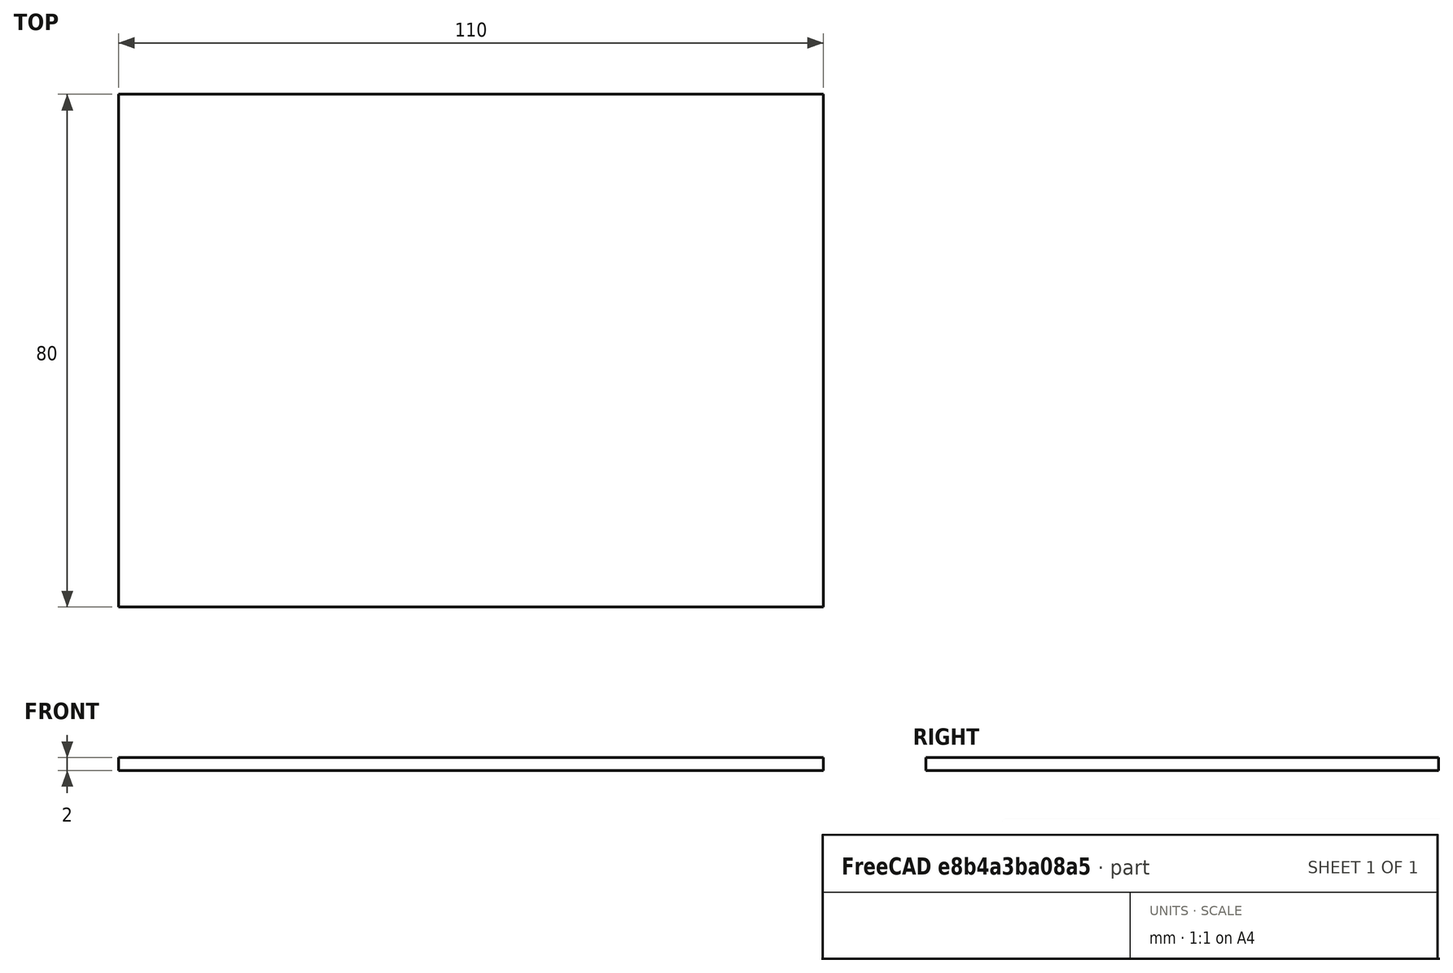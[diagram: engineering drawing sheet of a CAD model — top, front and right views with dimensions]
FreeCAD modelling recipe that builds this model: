
FCSTD DOCUMENT  (FreeCAD 0.18R16146 (Git))
Label: v_w-tapa-paso 1
License: All rights reserved
LicenseURL: http://en.wikipedia.org/wiki/All_rights_reserved
objects: Sketcher::SketchObject×1, PartDesign::Pad×1, PartDesign::Body×1
note: 4 computed .brp shape members not serialized (recipe doc carries the construction recipe); baked Part::Feature solids carry a one-line shape summary decoded from their .brp

FEATURE [Sketcher::SketchObject] Sketch
  MapMode = 5
  Support = -> [XY_Plane]
  sketch-geometry (4):
    g0: LineSegment StartX=-55 StartY=-40 StartZ=0 EndX=55 EndY=-40 EndZ=0
    g1: LineSegment StartX=55 StartY=-40 StartZ=0 EndX=55 EndY=40 EndZ=0
    g2: LineSegment StartX=55 StartY=40 StartZ=0 EndX=-55 EndY=40 EndZ=0
    g3: LineSegment StartX=-55 StartY=40 StartZ=0 EndX=-55 EndY=-40 EndZ=0
  constraints (12):
    c: Coincident(g0,g1)
    c: Coincident(g1,g2)
    c: Coincident(g2,g3)
    c: Coincident(g3,g0)
    c: Horizontal(g0)
    c: Horizontal(g2)
    c: Vertical(g1)
    c: Vertical(g3)
    c: DistanceX(g-1,g1) = 55
    c: DistanceY(g-1,g1) = 40
    c: DistanceX(g2,g2) = 110
    c: DistanceY(g1,g1) = 80
FEATURE [PartDesign::Pad] Pad
  Length = 2
  Length2 = 100
  Profile = -> Sketch
  Type = 0
FEATURE [PartDesign::Body] Body
  Group = -> [Sketch,Pad]
  Origin = -> Origin
  Tip = -> Pad
